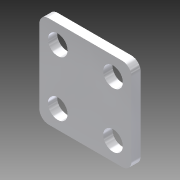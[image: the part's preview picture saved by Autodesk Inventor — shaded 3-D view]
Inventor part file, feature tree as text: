
AUTODESK INVENTOR PART (.ipt)
format: ipt  version: 2014 SP1 (Build 180222100, 222)  size: 114,176 bytes
history: native  units: in
note: dims shown in document units (in); Inventor stores cm internally (conversion verified against a paired STEP export)
features: extrude x1, fillet x1, sketch x1
ambient origin geometry x8: Origin, YZ Plane, XZ Plane, XY Plane, X Axis, Y Axis, Z Axis, Center Point
bodies: Solid1 (feature_tree)
feature tree (3):
  extrude  "Extrusion1"  Depth=1.25in
  fillet  "Fillet1"  Radius=0.266in
  sketch  "Sketch1"  dims[d0=1.25in d1=1.25in d2=0.266in d3=0.7874in d5=0.75in d6=0.7874in d8=0.75in d11=0.125in d12=0.0in d13=0.125in]
